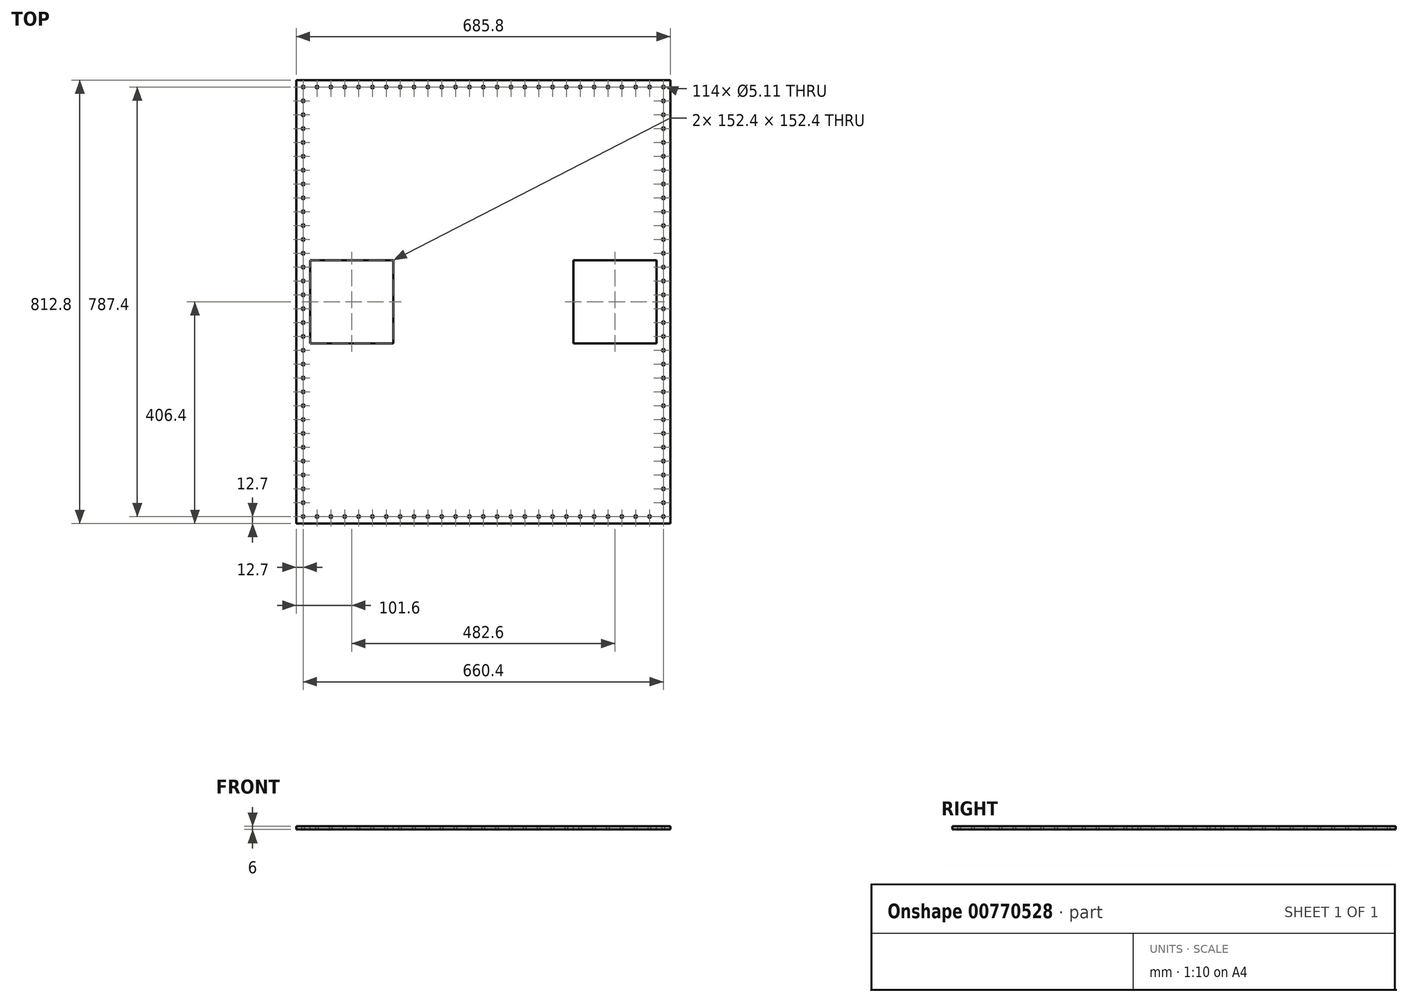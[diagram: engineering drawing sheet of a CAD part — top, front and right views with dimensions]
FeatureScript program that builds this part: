
annotation { "Feature Type Name" : "Feature", "Feature Type Description" : "" }
export const myFeature = defineFeature(function(context is Context, id is Id, definition is map)
    precondition{}
    {
        {
            var Q0;
            Q0=qCreatedBy(makeId("Top.planeOp"),FACE);
            var sketch = newSketch(context, id + "F0", { "sketchPlane" : qUnion([Q0])});
            skLineSegment(sketch, "E0.bottom", {"start": v(342.9, 406.4) * mm, "end": v(-342.9, 406.4) * mm});
            skLineSegment(sketch, "E0.top", {"start": v(342.9, -406.4) * mm, "end": v(-342.9, -406.4) * mm});
            skLineSegment(sketch, "E0.left", {"start": v(342.9, 406.4) * mm, "end": v(342.9, -406.4) * mm});
            skLineSegment(sketch, "E0.right", {"start": v(-342.9, 406.4) * mm, "end": v(-342.9, -406.4) * mm});
            skPoint(sketch, "E0.middle", {"position": v(0, 0) * mm});
            skSolve(sketch);
        }
        {
            var Q0;
            Q0=makeQuery(id+"F0.imprint","IMPRINT",FACE,{"disambiguationData":[TD([[makeQuery(id+"F0.imprint","IMPRINT",EDGE,{"derivedFrom":sQuery(id+"F0.wireOp",EDGE,"E0.bottom")}),1.0]])]});
            extrude(context, id + "F1", {"entities" : qUnion([Q0]), "depth" : 6 * mm, "offsetDistance" : 25.4 * mm});
        }
        {
            var Q0;
            Q0=makeQuery(id+"F1.opExtrude","CAP_FACE",FACE,{"disambiguationData":[OSD([sQuery(id+"F0.wireOp",EDGE,"E0.bottom"),sQuery(id+"F0.wireOp",EDGE,"E0.top"),sQuery(id+"F0.wireOp",EDGE,"E0.left"),sQuery(id+"F0.wireOp",EDGE,"E0.right")])],"isStart":false});
            var sketch = newSketch(context, id + "F2", { "sketchPlane" : qUnion([Q0])});
            skCircle(sketch, "E1", {"center": v(-330.2, 393.7) * mm, "radius": 2.55 * mm});
            skCircle(sketch, "E2.0.1.0", {"center": v(-330.2, 368.3) * mm, "radius": 2.55 * mm});
            skCircle(sketch, "E2.0.2.0", {"center": v(-330.2, 342.9) * mm, "radius": 2.55 * mm});
            skCircle(sketch, "E2.0.3.0", {"center": v(-330.2, 317.5) * mm, "radius": 2.55 * mm});
            skCircle(sketch, "E2.0.4.0", {"center": v(-330.2, 292.1) * mm, "radius": 2.55 * mm});
            skCircle(sketch, "E2.0.5.0", {"center": v(-330.2, 266.7) * mm, "radius": 2.55 * mm});
            skCircle(sketch, "E2.0.6.0", {"center": v(-330.2, 241.3) * mm, "radius": 2.55 * mm});
            skCircle(sketch, "E2.0.7.0", {"center": v(-330.2, 215.9) * mm, "radius": 2.55 * mm});
            skCircle(sketch, "E2.0.8.0", {"center": v(-330.2, 190.5) * mm, "radius": 2.55 * mm});
            skCircle(sketch, "E2.0.9.0", {"center": v(-330.2, 165.1) * mm, "radius": 2.55 * mm});
            skCircle(sketch, "E2.0.10.0", {"center": v(-330.2, 139.7) * mm, "radius": 2.55 * mm});
            skCircle(sketch, "E2.0.11.0", {"center": v(-330.2, 114.3) * mm, "radius": 2.55 * mm});
            skCircle(sketch, "E2.0.12.0", {"center": v(-330.2, 88.9) * mm, "radius": 2.55 * mm});
            skCircle(sketch, "E2.0.13.0", {"center": v(-330.2, 63.5) * mm, "radius": 2.55 * mm});
            skCircle(sketch, "E2.0.14.0", {"center": v(-330.2, 38.1) * mm, "radius": 2.55 * mm});
            skCircle(sketch, "E2.0.15.0", {"center": v(-330.2, 12.7) * mm, "radius": 2.55 * mm});
            skCircle(sketch, "E2.0.16.0", {"center": v(-330.2, -12.7) * mm, "radius": 2.55 * mm});
            skCircle(sketch, "E2.0.17.0", {"center": v(-330.2, -38.1) * mm, "radius": 2.55 * mm});
            skCircle(sketch, "E2.0.18.0", {"center": v(-330.2, -63.5) * mm, "radius": 2.55 * mm});
            skCircle(sketch, "E2.0.19.0", {"center": v(-330.2, -88.9) * mm, "radius": 2.55 * mm});
            skCircle(sketch, "E2.0.20.0", {"center": v(-330.2, -114.3) * mm, "radius": 2.55 * mm});
            skCircle(sketch, "E2.0.21.0", {"center": v(-330.2, -139.7) * mm, "radius": 2.55 * mm});
            skCircle(sketch, "E2.0.22.0", {"center": v(-330.2, -165.1) * mm, "radius": 2.55 * mm});
            skCircle(sketch, "E2.0.23.0", {"center": v(-330.2, -190.5) * mm, "radius": 2.55 * mm});
            skCircle(sketch, "E2.0.24.0", {"center": v(-330.2, -215.9) * mm, "radius": 2.55 * mm});
            skCircle(sketch, "E2.0.25.0", {"center": v(-330.2, -241.3) * mm, "radius": 2.55 * mm});
            skCircle(sketch, "E2.0.26.0", {"center": v(-330.2, -266.7) * mm, "radius": 2.55 * mm});
            skCircle(sketch, "E2.0.27.0", {"center": v(-330.2, -292.1) * mm, "radius": 2.55 * mm});
            skCircle(sketch, "E2.0.28.0", {"center": v(-330.2, -317.5) * mm, "radius": 2.55 * mm});
            skCircle(sketch, "E2.0.29.0", {"center": v(-330.2, -342.9) * mm, "radius": 2.55 * mm});
            skCircle(sketch, "E2.0.30.0", {"center": v(-330.2, -368.3) * mm, "radius": 2.55 * mm});
            skCircle(sketch, "E2.0.31.0", {"center": v(-330.2, -393.7) * mm, "radius": 2.55 * mm});
            skLineSegment(sketch, "E2.direction2", {"start": v(-330.2, 393.7) * mm, "end": v(-330.2, 368.3) * mm, "construction": true});
            skLineSegment(sketch, "E3.direction1", {"start": v(-330.2, -393.7) * mm, "end": v(-304.8, -393.7) * mm, "construction": true});
            skCircle(sketch, "E4.0.1.0", {"center": v(-304.8, -393.7) * mm, "radius": 2.55 * mm});
            skCircle(sketch, "E4.0.2.0", {"center": v(-279.4, -393.7) * mm, "radius": 2.55 * mm});
            skCircle(sketch, "E4.0.3.0", {"center": v(-254, -393.7) * mm, "radius": 2.55 * mm});
            skCircle(sketch, "E4.0.4.0", {"center": v(-228.6, -393.7) * mm, "radius": 2.55 * mm});
            skCircle(sketch, "E4.0.5.0", {"center": v(-203.2, -393.7) * mm, "radius": 2.55 * mm});
            skCircle(sketch, "E4.0.6.0", {"center": v(-177.8, -393.7) * mm, "radius": 2.55 * mm});
            skCircle(sketch, "E4.0.7.0", {"center": v(-152.4, -393.7) * mm, "radius": 2.55 * mm});
            skCircle(sketch, "E4.0.8.0", {"center": v(-127, -393.7) * mm, "radius": 2.55 * mm});
            skCircle(sketch, "E4.0.9.0", {"center": v(-101.6, -393.7) * mm, "radius": 2.55 * mm});
            skCircle(sketch, "E4.0.10.0", {"center": v(-76.2, -393.7) * mm, "radius": 2.55 * mm});
            skCircle(sketch, "E4.0.11.0", {"center": v(-50.8, -393.7) * mm, "radius": 2.55 * mm});
            skCircle(sketch, "E4.0.12.0", {"center": v(-25.4, -393.7) * mm, "radius": 2.55 * mm});
            skCircle(sketch, "E4.0.13.0", {"center": v(0, -393.7) * mm, "radius": 2.55 * mm});
            skCircle(sketch, "E4.0.14.0", {"center": v(25.4, -393.7) * mm, "radius": 2.55 * mm});
            skCircle(sketch, "E4.0.15.0", {"center": v(50.8, -393.7) * mm, "radius": 2.55 * mm});
            skCircle(sketch, "E4.0.16.0", {"center": v(76.2, -393.7) * mm, "radius": 2.55 * mm});
            skCircle(sketch, "E4.0.17.0", {"center": v(101.6, -393.7) * mm, "radius": 2.55 * mm});
            skCircle(sketch, "E4.0.18.0", {"center": v(127, -393.7) * mm, "radius": 2.55 * mm});
            skCircle(sketch, "E4.0.19.0", {"center": v(152.4, -393.7) * mm, "radius": 2.55 * mm});
            skCircle(sketch, "E4.0.20.0", {"center": v(177.8, -393.7) * mm, "radius": 2.55 * mm});
            skCircle(sketch, "E4.0.21.0", {"center": v(203.2, -393.7) * mm, "radius": 2.55 * mm});
            skCircle(sketch, "E4.0.22.0", {"center": v(228.6, -393.7) * mm, "radius": 2.55 * mm});
            skCircle(sketch, "E4.0.23.0", {"center": v(254, -393.7) * mm, "radius": 2.55 * mm});
            skCircle(sketch, "E4.0.24.0", {"center": v(279.4, -393.7) * mm, "radius": 2.55 * mm});
            skCircle(sketch, "E4.0.25.0", {"center": v(304.8, -393.7) * mm, "radius": 2.55 * mm});
            skCircle(sketch, "E4.0.26.0", {"center": v(330.2, -393.7) * mm, "radius": 2.55 * mm});
            skCircle(sketch, "E5.1.0.0", {"center": v(-304.8, 393.7) * mm, "radius": 2.55 * mm});
            skCircle(sketch, "E5.2.0.0", {"center": v(-279.4, 393.7) * mm, "radius": 2.55 * mm});
            skCircle(sketch, "E5.3.0.0", {"center": v(-254, 393.7) * mm, "radius": 2.55 * mm});
            skCircle(sketch, "E5.4.0.0", {"center": v(-228.6, 393.7) * mm, "radius": 2.55 * mm});
            skCircle(sketch, "E5.5.0.0", {"center": v(-203.2, 393.7) * mm, "radius": 2.55 * mm});
            skCircle(sketch, "E5.6.0.0", {"center": v(-177.8, 393.7) * mm, "radius": 2.55 * mm});
            skCircle(sketch, "E5.7.0.0", {"center": v(-152.4, 393.7) * mm, "radius": 2.55 * mm});
            skCircle(sketch, "E5.8.0.0", {"center": v(-127, 393.7) * mm, "radius": 2.55 * mm});
            skCircle(sketch, "E5.9.0.0", {"center": v(-101.6, 393.7) * mm, "radius": 2.55 * mm});
            skCircle(sketch, "E5.10.0.0", {"center": v(-76.2, 393.7) * mm, "radius": 2.55 * mm});
            skCircle(sketch, "E5.11.0.0", {"center": v(-50.8, 393.7) * mm, "radius": 2.55 * mm});
            skCircle(sketch, "E5.12.0.0", {"center": v(-25.4, 393.7) * mm, "radius": 2.55 * mm});
            skCircle(sketch, "E5.13.0.0", {"center": v(0, 393.7) * mm, "radius": 2.55 * mm});
            skCircle(sketch, "E5.14.0.0", {"center": v(25.4, 393.7) * mm, "radius": 2.55 * mm});
            skCircle(sketch, "E5.15.0.0", {"center": v(50.8, 393.7) * mm, "radius": 2.55 * mm});
            skCircle(sketch, "E5.16.0.0", {"center": v(76.2, 393.7) * mm, "radius": 2.55 * mm});
            skCircle(sketch, "E5.17.0.0", {"center": v(101.6, 393.7) * mm, "radius": 2.55 * mm});
            skCircle(sketch, "E5.18.0.0", {"center": v(127, 393.7) * mm, "radius": 2.55 * mm});
            skCircle(sketch, "E5.19.0.0", {"center": v(152.4, 393.7) * mm, "radius": 2.55 * mm});
            skCircle(sketch, "E5.20.0.0", {"center": v(177.8, 393.7) * mm, "radius": 2.55 * mm});
            skCircle(sketch, "E5.21.0.0", {"center": v(203.2, 393.7) * mm, "radius": 2.55 * mm});
            skCircle(sketch, "E5.22.0.0", {"center": v(228.6, 393.7) * mm, "radius": 2.55 * mm});
            skCircle(sketch, "E5.23.0.0", {"center": v(254, 393.7) * mm, "radius": 2.55 * mm});
            skCircle(sketch, "E5.24.0.0", {"center": v(279.4, 393.7) * mm, "radius": 2.55 * mm});
            skCircle(sketch, "E5.25.0.0", {"center": v(304.8, 393.7) * mm, "radius": 2.55 * mm});
            skCircle(sketch, "E5.26.0.0", {"center": v(330.2, 393.7) * mm, "radius": 2.55 * mm});
            skLineSegment(sketch, "E5.direction1", {"start": v(-330.2, 393.7) * mm, "end": v(-304.8, 393.7) * mm, "construction": true});
            skCircle(sketch, "E6.0.1.0", {"center": v(330.2, 368.3) * mm, "radius": 2.55 * mm});
            skCircle(sketch, "E6.0.2.0", {"center": v(330.2, 342.9) * mm, "radius": 2.55 * mm});
            skCircle(sketch, "E6.0.3.0", {"center": v(330.2, 317.5) * mm, "radius": 2.55 * mm});
            skCircle(sketch, "E6.0.4.0", {"center": v(330.2, 292.1) * mm, "radius": 2.55 * mm});
            skCircle(sketch, "E6.0.5.0", {"center": v(330.2, 266.7) * mm, "radius": 2.55 * mm});
            skCircle(sketch, "E6.0.6.0", {"center": v(330.2, 241.3) * mm, "radius": 2.55 * mm});
            skCircle(sketch, "E6.0.7.0", {"center": v(330.2, 215.9) * mm, "radius": 2.55 * mm});
            skCircle(sketch, "E6.0.8.0", {"center": v(330.2, 190.5) * mm, "radius": 2.55 * mm});
            skCircle(sketch, "E6.0.9.0", {"center": v(330.2, 165.1) * mm, "radius": 2.55 * mm});
            skCircle(sketch, "E6.0.10.0", {"center": v(330.2, 139.7) * mm, "radius": 2.55 * mm});
            skCircle(sketch, "E6.0.11.0", {"center": v(330.2, 114.3) * mm, "radius": 2.55 * mm});
            skCircle(sketch, "E6.0.12.0", {"center": v(330.2, 88.9) * mm, "radius": 2.55 * mm});
            skCircle(sketch, "E6.0.13.0", {"center": v(330.2, 63.5) * mm, "radius": 2.55 * mm});
            skCircle(sketch, "E6.0.14.0", {"center": v(330.2, 38.1) * mm, "radius": 2.55 * mm});
            skCircle(sketch, "E6.0.15.0", {"center": v(330.2, 12.7) * mm, "radius": 2.55 * mm});
            skCircle(sketch, "E6.0.16.0", {"center": v(330.2, -12.7) * mm, "radius": 2.55 * mm});
            skCircle(sketch, "E6.0.17.0", {"center": v(330.2, -38.1) * mm, "radius": 2.55 * mm});
            skCircle(sketch, "E6.0.18.0", {"center": v(330.2, -63.5) * mm, "radius": 2.55 * mm});
            skCircle(sketch, "E6.0.19.0", {"center": v(330.2, -88.9) * mm, "radius": 2.55 * mm});
            skCircle(sketch, "E6.0.20.0", {"center": v(330.2, -114.3) * mm, "radius": 2.55 * mm});
            skCircle(sketch, "E6.0.21.0", {"center": v(330.2, -139.7) * mm, "radius": 2.55 * mm});
            skCircle(sketch, "E6.0.22.0", {"center": v(330.2, -165.1) * mm, "radius": 2.55 * mm});
            skCircle(sketch, "E6.0.23.0", {"center": v(330.2, -190.5) * mm, "radius": 2.55 * mm});
            skCircle(sketch, "E6.0.24.0", {"center": v(330.2, -215.9) * mm, "radius": 2.55 * mm});
            skCircle(sketch, "E6.0.25.0", {"center": v(330.2, -241.3) * mm, "radius": 2.55 * mm});
            skCircle(sketch, "E6.0.26.0", {"center": v(330.2, -266.7) * mm, "radius": 2.55 * mm});
            skCircle(sketch, "E6.0.27.0", {"center": v(330.2, -292.1) * mm, "radius": 2.55 * mm});
            skCircle(sketch, "E6.0.28.0", {"center": v(330.2, -317.5) * mm, "radius": 2.55 * mm});
            skCircle(sketch, "E6.0.29.0", {"center": v(330.2, -342.9) * mm, "radius": 2.55 * mm});
            skCircle(sketch, "E6.0.30.0", {"center": v(330.2, -368.3) * mm, "radius": 2.55 * mm});
            skLineSegment(sketch, "E6.direction1", {"start": v(330.2, 393.7) * mm, "end": v(355.6, 393.7) * mm, "construction": true});
            skLineSegment(sketch, "E6.direction2", {"start": v(330.2, 393.7) * mm, "end": v(330.2, 368.3) * mm, "construction": true});
            skSolve(sketch);
        }
        {
            var Q0;
            Q0 = qSketchRegion(id + "F2", true);
            extrude(context, id + "F3", {"entities" : qUnion([Q0]), "operationType" : NewBodyOperationType.REMOVE, "oppositeDirection" : true, "depth" : 25.4 * mm, "offsetDistance" : 25.4 * mm});
        }
        {
            var Q0;
            Q0=makeQuery(id+"F1.opExtrude","CAP_FACE",FACE,{"disambiguationData":[OSD([sQuery(id+"F0.wireOp",EDGE,"E0.bottom"),sQuery(id+"F0.wireOp",EDGE,"E0.top"),sQuery(id+"F0.wireOp",EDGE,"E0.left"),sQuery(id+"F0.wireOp",EDGE,"E0.right")])],"isStart":false});
            var sketch = newSketch(context, id + "F4", { "sketchPlane" : qUnion([Q0])});
            skLineSegment(sketch, "E7.bottom", {"start": v(-317.5, 76.2) * mm, "end": v(-165.1, 76.2) * mm});
            skLineSegment(sketch, "E7.top", {"start": v(-317.5, -76.2) * mm, "end": v(-165.1, -76.2) * mm});
            skLineSegment(sketch, "E7.left", {"start": v(-317.5, 76.2) * mm, "end": v(-317.5, -76.2) * mm});
            skLineSegment(sketch, "E7.right", {"start": v(-165.1, 76.2) * mm, "end": v(-165.1, -76.2) * mm});
            skPoint(sketch, "E7.middle", {"position": v(-241.3, 0) * mm});
            skLineSegment(sketch, "E8.bottom", {"start": v(317.5, -76.2) * mm, "end": v(165.1, -76.2) * mm});
            skLineSegment(sketch, "E8.top", {"start": v(317.5, 76.2) * mm, "end": v(165.1, 76.2) * mm});
            skLineSegment(sketch, "E8.left", {"start": v(317.5, -76.2) * mm, "end": v(317.5, 76.2) * mm});
            skLineSegment(sketch, "E8.right", {"start": v(165.1, -76.2) * mm, "end": v(165.1, 76.2) * mm});
            skPoint(sketch, "E8.middle", {"position": v(241.3, 0) * mm});
            skSolve(sketch);
        }
        {
            var Q0;
            Q0 = qSketchRegion(id + "F4", true);
            extrude(context, id + "F5", {"entities" : qUnion([Q0]), "operationType" : NewBodyOperationType.REMOVE, "endBound" : BoundingType.THROUGH_ALL, "oppositeDirection" : true, "depth" : 25.4 * mm, "offsetDistance" : 25.4 * mm});
        }
    });
